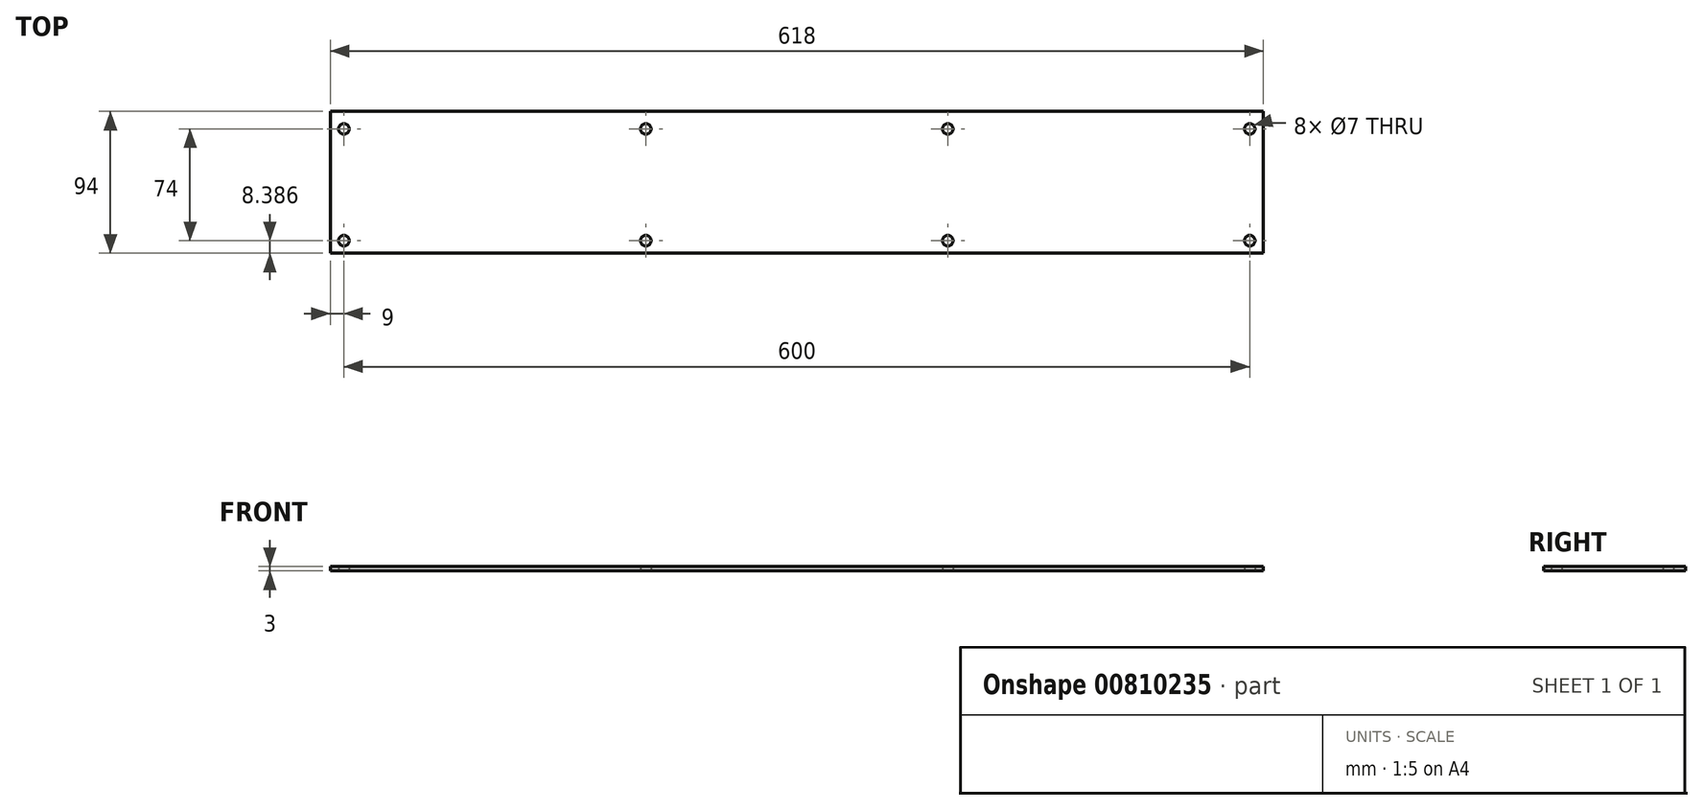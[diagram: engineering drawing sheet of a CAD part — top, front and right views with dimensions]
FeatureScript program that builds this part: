
annotation { "Feature Type Name" : "Feature", "Feature Type Description" : "" }
export const myFeature = defineFeature(function(context is Context, id is Id, definition is map)
    precondition{}
    {
        {
            var Q0;
            Q0=qCreatedBy(makeId("Top.planeOp"),FACE);
            var sketch = newSketch(context, id + "F0", { "sketchPlane" : qUnion([Q0])});
            skLineSegment(sketch, "E0.bottom", {"start": v(309, 47) * mm, "end": v(-309, 47) * mm});
            skLineSegment(sketch, "E0.top", {"start": v(309, -47) * mm, "end": v(-309, -47) * mm});
            skLineSegment(sketch, "E0.left", {"start": v(309, 47) * mm, "end": v(309, -47) * mm});
            skLineSegment(sketch, "E0.right", {"start": v(-309, 47) * mm, "end": v(-309, -47) * mm});
            skPoint(sketch, "E0.middle", {"position": v(0, 0) * mm});
            skLineSegment(sketch, "E1", {"start": v(0, -63.28) * mm, "end": v(0, 60.83) * mm, "construction": true});
            skCircle(sketch, "E2", {"center": v(-300, 35.39) * mm, "radius": 3.5 * mm});
            skCircle(sketch, "E3", {"center": v(-100, 35.39) * mm, "radius": 3.5 * mm});
            skCircle(sketch, "E4", {"center": v(100, 35.39) * mm, "radius": 3.5 * mm});
            skCircle(sketch, "E5", {"center": v(300, 35.39) * mm, "radius": 3.5 * mm});
            skCircle(sketch, "E6", {"center": v(300, -38.61) * mm, "radius": 3.5 * mm});
            skCircle(sketch, "E7", {"center": v(100, -38.61) * mm, "radius": 3.5 * mm});
            skCircle(sketch, "E8", {"center": v(-100, -38.61) * mm, "radius": 3.5 * mm});
            skCircle(sketch, "E9", {"center": v(-300, -38.61) * mm, "radius": 3.5 * mm});
            skSolve(sketch);
        }
        {
            var Q0;
            Q0=makeQuery(id+"F0.imprint","IMPRINT",FACE,{"disambiguationData":[TD([[makeQuery(id+"F0.imprint","IMPRINT",EDGE,{"derivedFrom":sQuery(id+"F0.wireOp",EDGE,"E0.bottom")}),1.0]])]});
            extrude(context, id + "F1", {"entities" : qUnion([Q0]), "depth" : 3 * mm, "offsetDistance" : 25 * mm});
        }
    });
